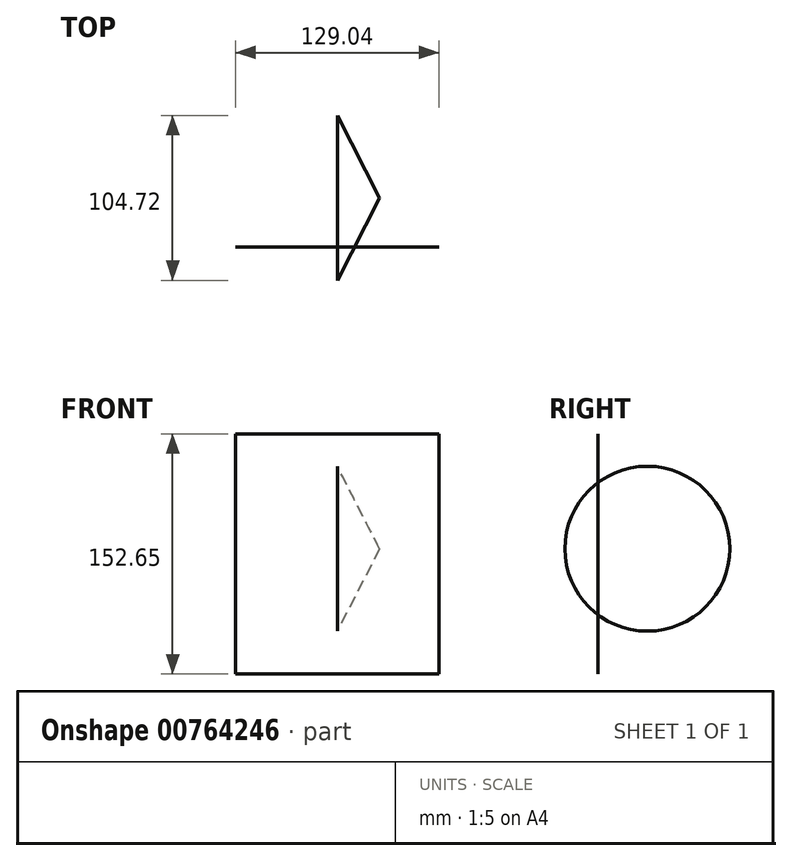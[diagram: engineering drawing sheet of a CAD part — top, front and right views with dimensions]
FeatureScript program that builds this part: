
annotation { "Feature Type Name" : "Feature", "Feature Type Description" : "" }
export const myFeature = defineFeature(function(context is Context, id is Id, definition is map)
    precondition{}
    {
        {
            var Q0;
            Q0=qCreatedBy(makeId("Front.planeOp"),FACE);
            var sketch = newSketch(context, id + "F0", { "sketchPlane" : qUnion([Q0])});
            skLineSegment(sketch, "E0", {"start": v(0, 3.41) * mm, "end": v(26.84, 3.41) * mm});
            skLineSegment(sketch, "E1", {"start": v(26.84, 3.41) * mm, "end": v(0, 55.77) * mm});
            skLineSegment(sketch, "E2", {"start": v(0, 55.77) * mm, "end": v(0, 3.41) * mm});
            skSolve(sketch);
        }
        {
            var Q0;
            Q0=sQuery(id+"F0.wireOp",EDGE,"E1");
            var Q1;
            Q1=sQuery(id+"F0.wireOp",EDGE,"E0");
            revolve(context, id + "F1", {"bodyType" : ToolBodyType.SURFACE, "surfaceOperationType" : NewSurfaceOperationType.NEW, "surfaceEntities" : qUnion([Q0]), "axis" : qUnion([Q1]), "revolveType" : RevolveType.FULL});
        }
        {
            var Q0;
            Q0=qCreatedBy(makeId("Right.planeOp"),FACE);
            var sketch = newSketch(context, id + "F2", { "sketchPlane" : qUnion([Q0])});
            skLineSegment(sketch, "E3", {"start": v(-31.25, 76.42) * mm, "end": v(-31.25, -76.23) * mm});
            skSolve(sketch);
        }
        {
            var Q0;
            Q0 = qSketchRegion(id + "F2", true);
            var Q1;
            Q1=sQuery(id+"F2.wireOp",EDGE,"E3");
            extrude(context, id + "F3", {"entities" : qUnion([Q0]), "bodyType" : ToolBodyType.SURFACE, "surfaceEntities" : qUnion([Q1]), "endBound" : BoundingType.SYMMETRIC, "oppositeDirection" : true, "depth" : 129.03 * mm, "offsetDistance" : 25.4 * mm});
        }
    });
